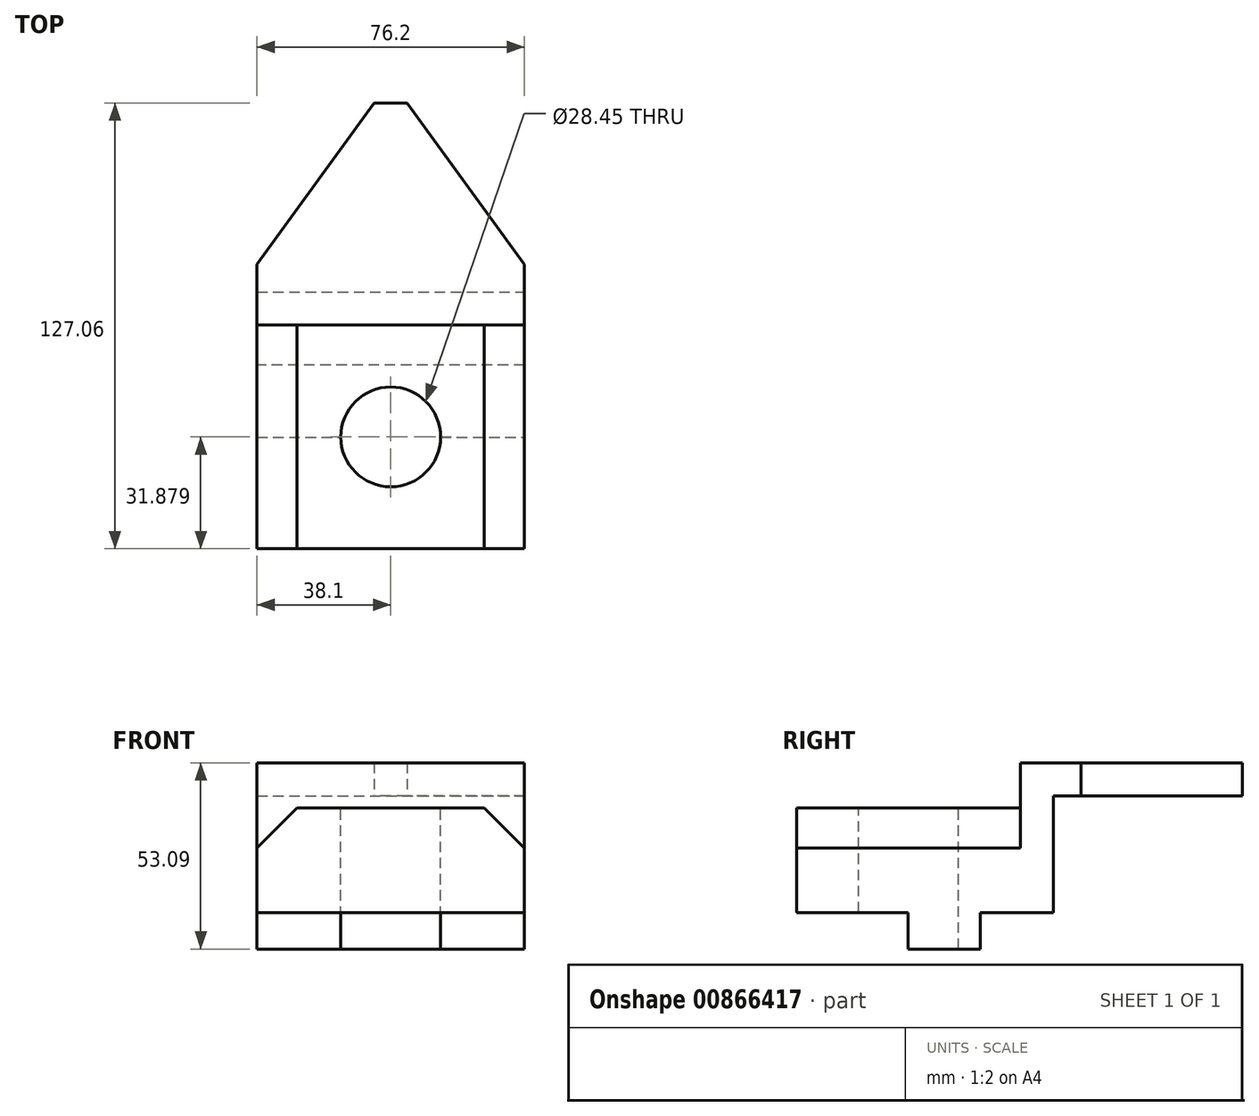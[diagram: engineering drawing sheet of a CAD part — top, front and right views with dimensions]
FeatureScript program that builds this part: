
annotation { "Feature Type Name" : "Feature", "Feature Type Description" : "" }
export const myFeature = defineFeature(function(context is Context, id is Id, definition is map)
    precondition{}
    {
        {
            var Q0;
            Q0=qCreatedBy(makeId("Top.planeOp"),FACE);
            var sketch = newSketch(context, id + "F0", { "sketchPlane" : qUnion([Q0])});
            skLineSegment(sketch, "E0", {"start": v(-69.82, 21.13) * mm, "end": v(6.38, 21.13) * mm});
            skLineSegment(sketch, "E1", {"start": v(6.38, 21.13) * mm, "end": v(6.38, 38.46) * mm});
            skLineSegment(sketch, "E2", {"start": v(6.38, 38.46) * mm, "end": v(-27.02, 84.43) * mm});
            skLineSegment(sketch, "E3", {"start": v(-27.02, 84.43) * mm, "end": v(-36.42, 84.43) * mm});
            skLineSegment(sketch, "E4", {"start": v(-69.82, 21.13) * mm, "end": v(-69.82, 38.46) * mm});
            skLineSegment(sketch, "E5", {"start": v(-69.82, 38.46) * mm, "end": v(-36.42, 84.43) * mm});
            skSolve(sketch);
        }
        {
            var Q0;
            Q0 = qSketchRegion(id + "F0", true);
            extrude(context, id + "F1", {"entities" : qUnion([Q0]), "depth" : 9.4 * mm, "offsetDistance" : 25.4 * mm});
        }
        {
            var Q0;
            Q0=makeQuery(id+"F1.opExtrude","SWEPT_FACE",FACE,{"disambiguationData":[OSD([sQuery(id+"F0.wireOp",EDGE,"E0")])]});
            var sketch = newSketch(context, id + "F2", { "sketchPlane" : qUnion([Q0])});
            skLineSegment(sketch, "E6.bottom", {"start": v(-69.82, 0) * mm, "end": v(6.38, 0) * mm});
            skLineSegment(sketch, "E6.top", {"start": v(-69.82, -33.27) * mm, "end": v(6.38, -33.27) * mm});
            skLineSegment(sketch, "E6.left", {"start": v(-69.82, 0) * mm, "end": v(-69.82, -33.27) * mm});
            skLineSegment(sketch, "E6.right", {"start": v(6.38, 0) * mm, "end": v(6.38, -33.27) * mm});
            skSolve(sketch);
        }
        {
            var Q0;
            Q0 = qSketchRegion(id + "F2", true);
            extrude(context, id + "F3", {"entities" : qUnion([Q0]), "operationType" : NewBodyOperationType.ADD, "oppositeDirection" : true, "depth" : 9.4 * mm, "offsetDistance" : 25.4 * mm});
        }
        {
            var Q0;
            Q0=makeQuery(id+"F3.boolean.opBoolean","MERGE",FACE,{"derivedFrom":[makeQuery(id+"F1.opExtrude","SWEPT_FACE",FACE,{"disambiguationData":[OSD([sQuery(id+"F0.wireOp",EDGE,"E0")])]}),makeQuery(id+"F3.opExtrude","CAP_FACE",FACE,{"disambiguationData":[OSD([sQuery(id+"F2.wireOp",EDGE,"E6.bottom"),sQuery(id+"F2.wireOp",EDGE,"E6.top"),sQuery(id+"F2.wireOp",EDGE,"E6.left"),sQuery(id+"F2.wireOp",EDGE,"E6.right")])],"isStart":true})]});
            var sketch = newSketch(context, id + "F4", { "sketchPlane" : qUnion([Q0])});
            skLineSegment(sketch, "E7", {"start": v(-69.82, -3.49) * mm, "end": v(6.38, -3.49) * mm});
            skSolve(sketch);
        }
        {
            var Q0;
            {var subQ0=sQuery(id+"F4.wireOp",EDGE,"E7");Q0=makeQuery(id+"F4.imprint","IMPRINT",FACE,{"disambiguationData":[TD([[makeQuery(id+"F4.imprint","IMPRINT",EDGE,{"derivedFrom":subQ0}),-1.0]])]});}
            extrude(context, id + "F5", {"entities" : qUnion([Q0]), "operationType" : NewBodyOperationType.ADD, "depth" : 63.75 * mm, "offsetDistance" : 25.4 * mm});
        }
        {
            var Q0;
            Q0=makeQuery(id+"F5.opExtrude","SWEPT_EDGE",EDGE,{"disambiguationData":[OSD([sQuery(id+"F0.wireOp",EDGE,"E0"),sQuery(id+"F0.wireOp",EDGE,"E1"),sQuery(id+"F2.wireOp",EDGE,"E6.right"),sQuery(id+"F4.wireOp",EDGE,"E7")])]});
            var Q1;
            Q1=makeQuery(id+"F5.opExtrude","SWEPT_EDGE",EDGE,{"disambiguationData":[OSD([sQuery(id+"F0.wireOp",EDGE,"E0"),sQuery(id+"F0.wireOp",EDGE,"E4"),sQuery(id+"F2.wireOp",EDGE,"E6.left"),sQuery(id+"F4.wireOp",EDGE,"E7")])]});
            chamfer(context, id + "F6", {"entities" : qUnion([Q0, Q1]), "width" : 11.43 * mm, "tangentPropagation" : true});
        }
        {
            var Q0;
            {var subQ0=sQuery(id+"F2.wireOp",EDGE,"E6.top");Q0=makeQuery(id+"F5.boolean.opBoolean","MERGE",FACE,{"derivedFrom":[makeQuery(id+"F3.opExtrude","SWEPT_FACE",FACE,{"disambiguationData":[OSD([subQ0])]}),makeQuery(id+"F5.opExtrude","SWEPT_FACE",FACE,{"disambiguationData":[OSD([subQ0])]})]});}
            var sketch = newSketch(context, id + "F7", { "sketchPlane" : qUnion([Q0])});
            skLineSegment(sketch, "E8", {"start": v(-69.82, 10.88) * mm, "end": v(6.38, 10.88) * mm});
            skLineSegment(sketch, "E9", {"start": v(6.38, 10.88) * mm, "end": v(6.38, -9.7) * mm});
            skLineSegment(sketch, "E10", {"start": v(6.38, -9.7) * mm, "end": v(-69.82, -9.7) * mm});
            skLineSegment(sketch, "E11", {"start": v(-69.82, -9.7) * mm, "end": v(-69.82, 10.88) * mm});
            skSolve(sketch);
        }
        {
            var Q0;
            Q0=makeQuery(id+"F7.imprint","IMPRINT",FACE,{"disambiguationData":[TD([[makeQuery(id+"F7.imprint","IMPRINT",EDGE,{"derivedFrom":sQuery(id+"F7.wireOp",EDGE,"E8")}),-1.0]])]});
            extrude(context, id + "F8", {"entities" : qUnion([Q0]), "operationType" : NewBodyOperationType.ADD, "depth" : 10.4 * mm, "offsetDistance" : 25.4 * mm});
        }
        {
            var Q0;
            Q0=makeQuery(id+"F5.opExtrude","SWEPT_FACE",FACE,{"disambiguationData":[OSD([sQuery(id+"F4.wireOp",EDGE,"E7")])]});
            var sketch = newSketch(context, id + "F9", { "sketchPlane" : qUnion([Q0])});
            skCircle(sketch, "E12", {"center": v(-31.72, -10.75) * mm, "radius": 14.22 * mm});
            skPoint(sketch, "E12.centerSnap0", {"position": v(-5.05, -10.75) * mm});
            skPoint(sketch, "E12.centerSnap1", {"position": v(-31.72, 21.13) * mm});
            skSolve(sketch);
        }
        {
            var Q0;
            Q0=makeQuery(id+"F9.imprint","IMPRINT",FACE,{"disambiguationData":[TD([[makeQuery(id+"F9.imprint","IMPRINT",EDGE,{"derivedFrom":sQuery(id+"F9.wireOp",EDGE,"E12")}),1.0]])]});
            extrude(context, id + "F10", {"entities" : qUnion([Q0]), "operationType" : NewBodyOperationType.REMOVE, "oppositeDirection" : true, "depth" : 58.93 * mm, "offsetDistance" : 25.4 * mm});
        }
    });
